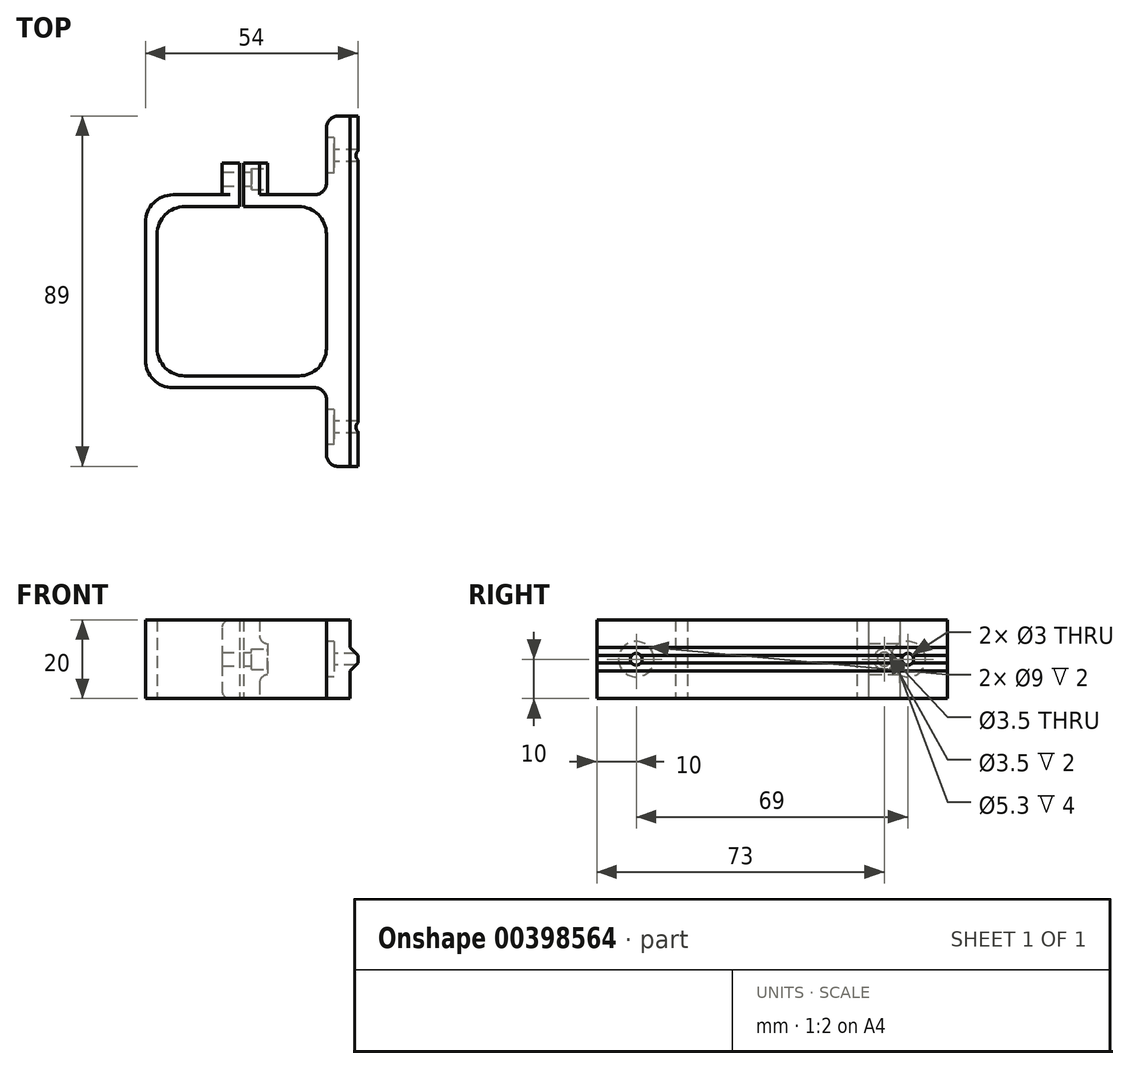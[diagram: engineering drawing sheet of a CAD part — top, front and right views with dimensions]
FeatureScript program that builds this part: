
annotation { "Feature Type Name" : "Feature", "Feature Type Description" : "" }
export const myFeature = defineFeature(function(context is Context, id is Id, definition is map)
    precondition{}
    {
        {
            var Q0;
            Q0=qCreatedBy(makeId("Top.planeOp"),FACE);
            var sketch = newSketch(context, id + "F0", { "sketchPlane" : qUnion([Q0])});
            skLineSegment(sketch, "E0.bottom", {"start": v(21.5, -21.5) * mm, "end": v(-21.5, -21.5) * mm});
            skLineSegment(sketch, "E0.top", {"start": v(21.5, 21.5) * mm, "end": v(0.5, 21.5) * mm});
            skLineSegment(sketch, "E0.left", {"start": v(21.5, -21.5) * mm, "end": v(21.5, 21.5) * mm});
            skLineSegment(sketch, "E0.right", {"start": v(-21.5, -21.5) * mm, "end": v(-21.5, 21.5) * mm});
            skPoint(sketch, "E0.middle", {"position": v(0, 0) * mm});
            skLineSegment(sketch, "E1.bottom", {"start": v(24.5, -24.5) * mm, "end": v(-24.5, -24.5) * mm});
            skLineSegment(sketch, "E1.top", {"start": v(24.5, 24.5) * mm, "end": v(0.5, 24.5) * mm});
            skLineSegment(sketch, "E1.left", {"start": v(24.5, -24.5) * mm, "end": v(24.5, 24.5) * mm});
            skLineSegment(sketch, "E1.right", {"start": v(-24.5, -24.5) * mm, "end": v(-24.5, 24.5) * mm});
            skLineSegment(sketch, "E2.bottom", {"start": v(27.5, -44.5) * mm, "end": v(21.5, -44.5) * mm});
            skLineSegment(sketch, "E2.top", {"start": v(27.5, 44.5) * mm, "end": v(21.5, 44.5) * mm});
            skLineSegment(sketch, "E2.left", {"start": v(27.5, -44.5) * mm, "end": v(27.5, 44.5) * mm});
            skLineSegment(sketch, "E2.right", {"start": v(21.5, -44.5) * mm, "end": v(21.5, 44.5) * mm});
            skPoint(sketch, "E2.middle", {"position": v(24.5, 0) * mm});
            skLineSegment(sketch, "E3.bottom", {"start": v(0.5, 24.5) * mm, "end": v(6.5, 24.5) * mm});
            skLineSegment(sketch, "E3.top", {"start": v(0.5, 32.5) * mm, "end": v(6.5, 32.5) * mm});
            skLineSegment(sketch, "E3.right", {"start": v(6.5, 24.5) * mm, "end": v(6.5, 32.5) * mm});
            skLineSegment(sketch, "E4.bottom", {"start": v(-0.5, 24.5) * mm, "end": v(-5, 24.5) * mm});
            skLineSegment(sketch, "E4.top", {"start": v(-0.5, 32.5) * mm, "end": v(-5, 32.5) * mm});
            skLineSegment(sketch, "E4.right", {"start": v(-5, 24.5) * mm, "end": v(-5, 32.5) * mm});
            skLineSegment(sketch, "E5.left", {"start": v(0.5, 21.5) * mm, "end": v(0.5, 27.5) * mm});
            skLineSegment(sketch, "E5.right", {"start": v(-0.5, 21.5) * mm, "end": v(-0.5, 27.5) * mm});
            skPoint(sketch, "E5.middle", {"position": v(0, 24.5) * mm});
            skLineSegment(sketch, "E6", {"start": v(-0.5, 27.5) * mm, "end": v(-0.5, 32.5) * mm});
            skLineSegment(sketch, "E7", {"start": v(0.5, 27.5) * mm, "end": v(0.5, 32.5) * mm});
            skLineSegment(sketch, "E8.trimOffspring", {"start": v(-0.5, 24.5) * mm, "end": v(-24.5, 24.5) * mm});
            skLineSegment(sketch, "E9.trimOffspring", {"start": v(-0.5, 21.5) * mm, "end": v(-21.5, 21.5) * mm});
            skSolve(sketch);
        }
        {
            var Q0;
            Q0 = qSketchRegion(id + "F0", true);
            extrude(context, id + "F1", {"entities" : qUnion([Q0]), "depth" : 20 * mm, "offsetDistance" : 25 * mm});
        }
        {
            var Q0;
            Q0=makeQuery(id+"F1.opExtrude","SWEPT_FACE",FACE,{"disambiguationData":[OSD([sQuery(id+"F0.wireOp",EDGE,"E3.right")])]});
            var sketch = newSketch(context, id + "F2", { "sketchPlane" : qUnion([Q0])});
            skPoint(sketch, "E10", {"position": v(28.5, 10) * mm});
            skPoint(sketch, "E10.positionSnap0", {"position": v(32.5, 10) * mm});
            skPoint(sketch, "E10.positionSnap1", {"position": v(28.5, 0) * mm});
            skLineSegment(sketch, "E11", {"start": v(32.5, 6) * mm, "end": v(24.5, 6) * mm});
            skLineSegment(sketch, "E12", {"start": v(24.5, 14) * mm, "end": v(32.5, 14) * mm});
            skSolve(sketch);
        }
        {
            var Q0;
            Q0=sQuery(id+"F2.wireOp",VERTEX,"E10");
            var Q1;
            Q1=makeQuery(id+"F1.opExtrude","SWEPT_BODY",BODY,{"disambiguationData":[OSD([sQuery(id+"F0.wireOp",EDGE,"E0.bottom"),sQuery(id+"F0.wireOp",EDGE,"E0.top"),sQuery(id+"F0.wireOp",EDGE,"E0.right"),sQuery(id+"F0.wireOp",EDGE,"E1.bottom"),sQuery(id+"F0.wireOp",EDGE,"E1.top"),sQuery(id+"F0.wireOp",EDGE,"E1.right"),sQuery(id+"F0.wireOp",EDGE,"E2.bottom"),sQuery(id+"F0.wireOp",EDGE,"E2.top"),sQuery(id+"F0.wireOp",EDGE,"E2.left"),sQuery(id+"F0.wireOp",EDGE,"E2.right"),sQuery(id+"F0.wireOp",EDGE,"E3.top"),sQuery(id+"F0.wireOp",EDGE,"E3.right"),sQuery(id+"F0.wireOp",EDGE,"E4.top"),sQuery(id+"F0.wireOp",EDGE,"E4.right"),sQuery(id+"F0.wireOp",EDGE,"E5.left"),sQuery(id+"F0.wireOp",EDGE,"E5.right"),sQuery(id+"F0.wireOp",EDGE,"E6"),sQuery(id+"F0.wireOp",EDGE,"E7"),sQuery(id+"F0.wireOp",EDGE,"E8.trimOffspring"),sQuery(id+"F0.wireOp",EDGE,"E9.trimOffspring")])]});
            hole(context, id + "F3", {"style" : HoleStyle.C_BORE, "endStyle" : HoleEndStyle.THROUGH, "holeDiameter" : 3.5 * mm, "cBoreDiameter" : 5.3 * mm, "cBoreDepth" : 4 * mm, "isTappedThrough" : true, "tappedDepth" : 12 * mm, "tapClearance" : 3, "locations" : qUnion([Q0]), "scope" : qUnion([Q1])});
        }
        {
            var Q0;
            {var subQ0=sQuery(id+"F2.wireOp",EDGE,"E12");Q0=makeQuery(id+"F2.imprint","IMPRINT",FACE,{"disambiguationData":[TD([[makeQuery(id+"F2.imprint","IMPRINT",EDGE,{"derivedFrom":subQ0}),1.0]])]});}
            var Q1;
            {var subQ0=sQuery(id+"F2.wireOp",EDGE,"E11");Q1=makeQuery(id+"F2.imprint","IMPRINT",FACE,{"disambiguationData":[TD([[makeQuery(id+"F2.imprint","IMPRINT",EDGE,{"derivedFrom":subQ0}),1.0]])]});}
            extrude(context, id + "F4", {"entities" : qUnion([Q0, Q1]), "operationType" : NewBodyOperationType.REMOVE, "oppositeDirection" : true, "depth" : 2 * mm, "offsetDistance" : 25 * mm});
        }
        {
            var Q0;
            Q0=makeQuery(id+"F4.boolean.opBoolean","COPY",EDGE,{"derivedFrom":makeQuery(id+"F4.opExtrude","CAP_EDGE",EDGE,{"disambiguationData":[OSD([sQuery(id+"F2.wireOp",EDGE,"E11")])],"isStart":false})});
            var Q1;
            Q1=makeQuery(id+"F4.boolean.opBoolean","COPY",EDGE,{"derivedFrom":makeQuery(id+"F4.opExtrude","CAP_EDGE",EDGE,{"disambiguationData":[OSD([sQuery(id+"F2.wireOp",EDGE,"E12")])],"isStart":false})});
            fillet(context, id + "F5", {"entities" : qUnion([Q0, Q1]), "radius" : 2 * mm, "tangentPropagation" : true, "allowEdgeOverflow" : false});
        }
        {
            var Q0;
            {var subQ0=sQuery(id+"F0.wireOp",EDGE,"E3.right");Q0=makeQuery(id+"F4.boolean.opBoolean","COPY",EDGE,{"derivedFrom":makeQuery(id+"F4.opExtrude","CAP_EDGE",EDGE,{"disambiguationData":[OSD([subQ0]),TDD([makeQuery(id+"F2.imprint","IMPRINT",EDGE,{"derivedFrom":makeQuery(id+"F1.opExtrude","CAP_EDGE",EDGE,{"disambiguationData":[OSD([subQ0])],"isStart":false})})])],"isStart":false})});}
            var Q1;
            Q1=makeQuery(id+"F1.opExtrude","CAP_EDGE",EDGE,{"disambiguationData":[OSD([sQuery(id+"F0.wireOp",EDGE,"E4.right")])],"isStart":false});
            var Q2;
            Q2=makeQuery(id+"F1.opExtrude","CAP_EDGE",EDGE,{"disambiguationData":[OSD([sQuery(id+"F0.wireOp",EDGE,"E4.right")])],"isStart":true});
            var Q3;
            {var subQ0=sQuery(id+"F0.wireOp",EDGE,"E3.right");Q3=makeQuery(id+"F4.boolean.opBoolean","COPY",EDGE,{"derivedFrom":makeQuery(id+"F4.opExtrude","CAP_EDGE",EDGE,{"disambiguationData":[OSD([subQ0]),TDD([makeQuery(id+"F2.imprint","IMPRINT",EDGE,{"derivedFrom":makeQuery(id+"F1.opExtrude","CAP_EDGE",EDGE,{"disambiguationData":[OSD([subQ0])],"isStart":true})})])],"isStart":false})});}
            fillet(context, id + "F6", {"entities" : qUnion([Q0, Q1, Q2, Q3]), "radius" : 2 * mm, "tangentPropagation" : true, "allowEdgeOverflow" : false});
        }
        {
            var Q0;
            Q0=makeQuery(id+"F1.opExtrude","SWEPT_EDGE",EDGE,{"disambiguationData":[OSD([sQuery(id+"F0.wireOp",EDGE,"E0.right"),sQuery(id+"F0.wireOp",EDGE,"E9.trimOffspring")])]});
            var Q1;
            Q1=makeQuery(id+"F1.opExtrude","SWEPT_EDGE",EDGE,{"disambiguationData":[OSD([sQuery(id+"F0.wireOp",EDGE,"E0.top"),sQuery(id+"F0.wireOp",EDGE,"E2.right")])]});
            var Q2;
            Q2=makeQuery(id+"F1.opExtrude","SWEPT_EDGE",EDGE,{"disambiguationData":[OSD([sQuery(id+"F0.wireOp",EDGE,"E0.bottom"),sQuery(id+"F0.wireOp",EDGE,"E0.right")])]});
            var Q3;
            Q3=makeQuery(id+"F1.opExtrude","SWEPT_EDGE",EDGE,{"disambiguationData":[OSD([sQuery(id+"F0.wireOp",EDGE,"E0.bottom"),sQuery(id+"F0.wireOp",EDGE,"E2.right")])]});
            var Q4;
            Q4=makeQuery(id+"F1.opExtrude","SWEPT_EDGE",EDGE,{"disambiguationData":[OSD([sQuery(id+"F0.wireOp",EDGE,"E1.right"),sQuery(id+"F0.wireOp",EDGE,"E8.trimOffspring")])]});
            var Q5;
            Q5=makeQuery(id+"F1.opExtrude","SWEPT_EDGE",EDGE,{"disambiguationData":[OSD([sQuery(id+"F0.wireOp",EDGE,"E1.bottom"),sQuery(id+"F0.wireOp",EDGE,"E1.right")])]});
            fillet(context, id + "F7", {"entities" : qUnion([Q0, Q1, Q2, Q3, Q4, Q5]), "radius" : 7 * mm, "tangentPropagation" : true, "allowEdgeOverflow" : false});
        }
        {
            var Q0;
            {var subQ0=sQuery(id+"F0.wireOp",EDGE,"E2.right");Q0=makeQuery(id+"F1.opExtrude","SWEPT_FACE",FACE,{"disambiguationData":[OSD([subQ0]),TDD([makeQuery(id+"F0.imprint","IMPRINT",EDGE,{"disambiguationData":[TD([[makeQuery(id+"F0.imprint","INTERSECT",VERTEX,{"derivedFrom":[sQuery(id+"F0.wireOp",EDGE,"E2.top"),subQ0]}),1.0]])],"derivedFrom":subQ0})])]});}
            var sketch = newSketch(context, id + "F8", { "sketchPlane" : qUnion([Q0])});
            skPoint(sketch, "E13", {"position": v(-34.5, 10) * mm});
            skPoint(sketch, "E13.positionSnap0", {"position": v(-44.5, 10) * mm});
            skPoint(sketch, "E13.positionSnap1", {"position": v(-34.5, 20) * mm});
            skSolve(sketch);
        }
        {
            var Q0;
            {var subQ0=sQuery(id+"F0.wireOp",EDGE,"E2.right");Q0=makeQuery(id+"F1.opExtrude","SWEPT_FACE",FACE,{"disambiguationData":[OSD([subQ0]),TDD([makeQuery(id+"F0.imprint","IMPRINT",EDGE,{"disambiguationData":[TD([[makeQuery(id+"F0.imprint","INTERSECT",VERTEX,{"derivedFrom":[sQuery(id+"F0.wireOp",EDGE,"E2.bottom"),subQ0]}),-1.0]])],"derivedFrom":subQ0})])]});}
            var sketch = newSketch(context, id + "F9", { "sketchPlane" : qUnion([Q0])});
            skPoint(sketch, "E14", {"position": v(34.5, 10) * mm});
            skPoint(sketch, "E14.positionSnap0", {"position": v(44.5, 10) * mm});
            skPoint(sketch, "E14.positionSnap1", {"position": v(34.5, 20) * mm});
            skSolve(sketch);
        }
        {
            var Q0;
            Q0=makeQuery(id+"F1.opExtrude","SWEPT_EDGE",EDGE,{"disambiguationData":[OSD([sQuery(id+"F0.wireOp",EDGE,"E2.bottom"),sQuery(id+"F0.wireOp",EDGE,"E2.right")])]});
            var Q1;
            Q1=makeQuery(id+"F1.opExtrude","SWEPT_EDGE",EDGE,{"disambiguationData":[OSD([sQuery(id+"F0.wireOp",EDGE,"E1.bottom"),sQuery(id+"F0.wireOp",EDGE,"E2.right")])]});
            var Q2;
            Q2=makeQuery(id+"F1.opExtrude","SWEPT_EDGE",EDGE,{"disambiguationData":[OSD([sQuery(id+"F0.wireOp",EDGE,"E1.top"),sQuery(id+"F0.wireOp",EDGE,"E2.right")])]});
            var Q3;
            Q3=makeQuery(id+"F1.opExtrude","SWEPT_EDGE",EDGE,{"disambiguationData":[OSD([sQuery(id+"F0.wireOp",EDGE,"E2.top"),sQuery(id+"F0.wireOp",EDGE,"E2.right")])]});
            fillet(context, id + "F10", {"entities" : qUnion([Q0, Q1, Q2, Q3]), "radius" : 3 * mm, "tangentPropagation" : true, "allowEdgeOverflow" : false});
        }
        {
            var Q0;
            Q0=sQuery(id+"F8.wireOp",VERTEX,"E13");
            var Q1;
            Q1=sQuery(id+"F9.wireOp",VERTEX,"E14");
            var Q2;
            Q2=makeQuery(id+"F1.opExtrude","SWEPT_BODY",BODY,{"disambiguationData":[OSD([sQuery(id+"F0.wireOp",EDGE,"E0.bottom"),sQuery(id+"F0.wireOp",EDGE,"E0.top"),sQuery(id+"F0.wireOp",EDGE,"E0.right"),sQuery(id+"F0.wireOp",EDGE,"E1.bottom"),sQuery(id+"F0.wireOp",EDGE,"E1.top"),sQuery(id+"F0.wireOp",EDGE,"E1.right"),sQuery(id+"F0.wireOp",EDGE,"E2.bottom"),sQuery(id+"F0.wireOp",EDGE,"E2.top"),sQuery(id+"F0.wireOp",EDGE,"E2.left"),sQuery(id+"F0.wireOp",EDGE,"E2.right"),sQuery(id+"F0.wireOp",EDGE,"E3.top"),sQuery(id+"F0.wireOp",EDGE,"E3.right"),sQuery(id+"F0.wireOp",EDGE,"E4.top"),sQuery(id+"F0.wireOp",EDGE,"E4.right"),sQuery(id+"F0.wireOp",EDGE,"E5.left"),sQuery(id+"F0.wireOp",EDGE,"E5.right"),sQuery(id+"F0.wireOp",EDGE,"E6"),sQuery(id+"F0.wireOp",EDGE,"E7"),sQuery(id+"F0.wireOp",EDGE,"E8.trimOffspring"),sQuery(id+"F0.wireOp",EDGE,"E9.trimOffspring")])]});
            hole(context, id + "F11", {"style" : HoleStyle.C_BORE, "endStyle" : HoleEndStyle.THROUGH, "holeDiameter" : 3 * mm, "cBoreDiameter" : 9 * mm, "cBoreDepth" : 2 * mm, "isTappedThrough" : true, "tappedDepth" : 12 * mm, "tapClearance" : 3, "locations" : qUnion([Q0, Q1]), "scope" : qUnion([Q2])});
        }
        {
            var Q0;
            Q0=makeQuery(id+"F1.opExtrude","SWEPT_FACE",FACE,{"disambiguationData":[OSD([sQuery(id+"F0.wireOp",EDGE,"E2.left")])]});
            var sketch = newSketch(context, id + "F12", { "sketchPlane" : qUnion([Q0])});
            skLineSegment(sketch, "E15.bottom", {"start": v(44.5, 7) * mm, "end": v(-44.5, 7) * mm});
            skLineSegment(sketch, "E15.top", {"start": v(44.5, 13) * mm, "end": v(-44.5, 13) * mm});
            skLineSegment(sketch, "E15.left", {"start": v(44.5, 7) * mm, "end": v(44.5, 13) * mm});
            skLineSegment(sketch, "E15.right", {"start": v(-44.5, 7) * mm, "end": v(-44.5, 13) * mm});
            skPoint(sketch, "E15.middle", {"position": v(0, 10) * mm});
            skPoint(sketch, "E15.middle.positionSnap0", {"position": v(44.5, 10) * mm});
            skPoint(sketch, "E15.centerSnap0", {"position": v(44.5, 10) * mm});
            skSolve(sketch);
        }
        {
            var Q0;
            Q0=makeQuery(id+"F12.imprint","IMPRINT",FACE,{"disambiguationData":[TD([[makeQuery(id+"F12.imprint","IMPRINT",EDGE,{"derivedFrom":sQuery(id+"F12.wireOp",EDGE,"E15.bottom")}),-1.0]])]});
            extrude(context, id + "F13", {"entities" : qUnion([Q0]), "operationType" : NewBodyOperationType.ADD, "depth" : 2 * mm, "offsetDistance" : 25 * mm});
        }
        {
            var Q0;
            Q0=makeQuery(id+"F13.opExtrude","CAP_EDGE",EDGE,{"disambiguationData":[OSD([sQuery(id+"F12.wireOp",EDGE,"E15.bottom")])],"isStart":false});
            var Q1;
            Q1=makeQuery(id+"F13.opExtrude","CAP_EDGE",EDGE,{"disambiguationData":[OSD([sQuery(id+"F12.wireOp",EDGE,"E15.top")])],"isStart":false});
            chamfer(context, id + "F14", {"entities" : qUnion([Q0, Q1]), "width" : 2 * mm, "tangentPropagation" : true});
        }
    });
